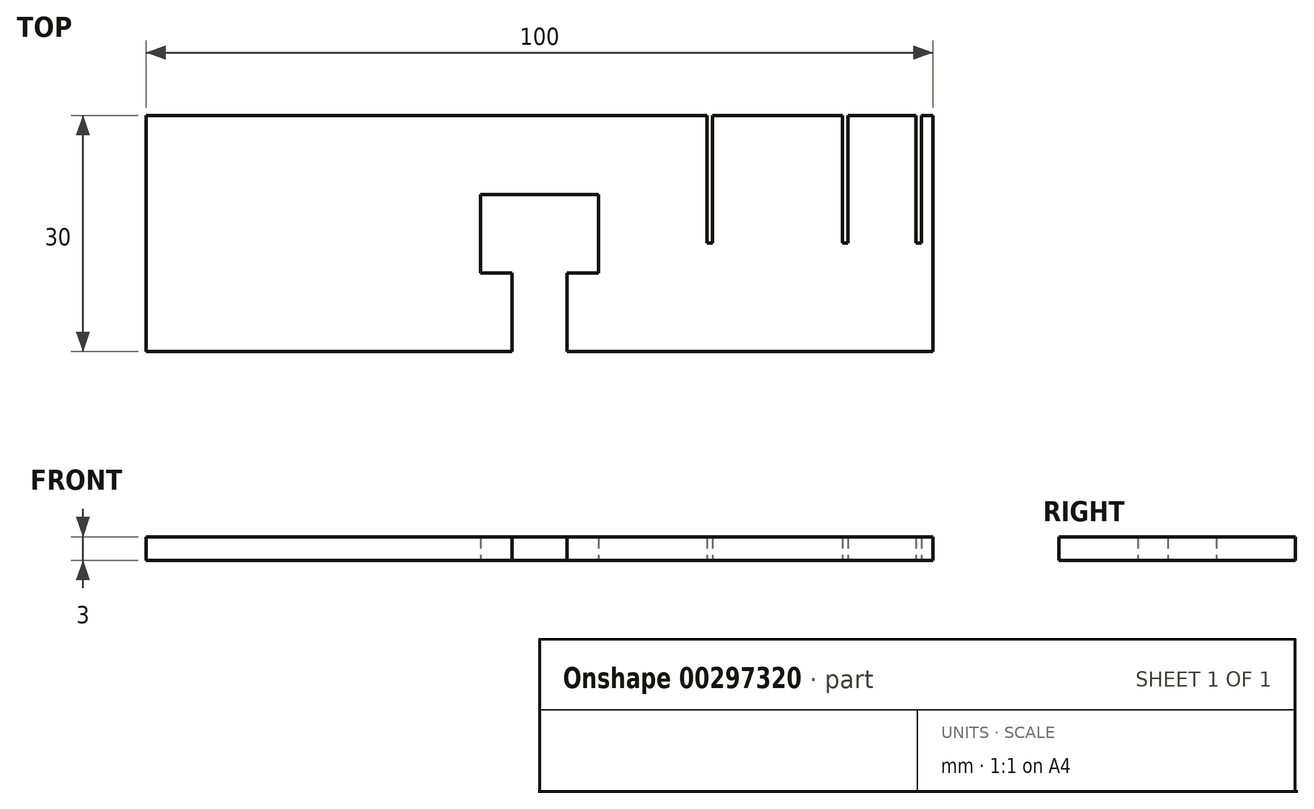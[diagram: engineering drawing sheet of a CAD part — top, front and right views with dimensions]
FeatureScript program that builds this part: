
annotation { "Feature Type Name" : "Feature", "Feature Type Description" : "" }
export const myFeature = defineFeature(function(context is Context, id is Id, definition is map)
    precondition{}
    {
        {
            var Q0;
            Q0=qCreatedBy(makeId("Top.planeOp"),FACE);
            var sketch = newSketch(context, id + "F0", { "sketchPlane" : qUnion([Q0])});
            skLineSegment(sketch, "E0.bottom", {"start": v(50, -15) * mm, "end": v(-50, -15) * mm});
            skLineSegment(sketch, "E0.top", {"start": v(50, 15) * mm, "end": v(-50, 15) * mm});
            skLineSegment(sketch, "E0.left", {"start": v(50, -15) * mm, "end": v(50, 15) * mm});
            skLineSegment(sketch, "E0.right", {"start": v(-50, -15) * mm, "end": v(-50, 15) * mm});
            skPoint(sketch, "E0.middle", {"position": v(0, 0) * mm});
            skSolve(sketch);
        }
        {
            var Q0;
            Q0=qCreatedBy(makeId("Top.planeOp"),FACE);
            var sketch = newSketch(context, id + "F1", { "sketchPlane" : qUnion([Q0])});
            skPoint(sketch, "E1.middle", {"position": v(0, 0) * mm});
            skLineSegment(sketch, "E2.bottom", {"start": v(7.5, -5) * mm, "end": v(-7.5, -5) * mm});
            skLineSegment(sketch, "E2.top", {"start": v(7.5, 5) * mm, "end": v(-7.5, 5) * mm});
            skLineSegment(sketch, "E2.left", {"start": v(7.5, -5) * mm, "end": v(7.5, 5) * mm});
            skLineSegment(sketch, "E2.right", {"start": v(-7.5, -5) * mm, "end": v(-7.5, 5) * mm});
            skLineSegment(sketch, "E3.bottom", {"start": v(-3.5, -5) * mm, "end": v(3.5, -5) * mm});
            skLineSegment(sketch, "E3.top", {"start": v(-3.5, -20) * mm, "end": v(3.5, -20) * mm});
            skLineSegment(sketch, "E3.left", {"start": v(-3.5, -5) * mm, "end": v(-3.5, -20) * mm});
            skLineSegment(sketch, "E3.right", {"start": v(3.5, -5) * mm, "end": v(3.5, -20) * mm});
            skLineSegment(sketch, "E4.bottom", {"start": v(21.3, -1.2) * mm, "end": v(22, -1.2) * mm});
            skLineSegment(sketch, "E4.top", {"start": v(21.3, 27.79) * mm, "end": v(22, 27.79) * mm});
            skLineSegment(sketch, "E4.left", {"start": v(21.3, -1.2) * mm, "end": v(21.3, 27.79) * mm});
            skLineSegment(sketch, "E4.right", {"start": v(22, -1.2) * mm, "end": v(22, 27.79) * mm});
            skLineSegment(sketch, "E5.bottom", {"start": v(47.8, -1.2) * mm, "end": v(48.5, -1.2) * mm});
            skLineSegment(sketch, "E5.top", {"start": v(47.8, 38.42) * mm, "end": v(48.5, 38.42) * mm});
            skLineSegment(sketch, "E5.left", {"start": v(47.8, -1.2) * mm, "end": v(47.8, 38.42) * mm});
            skLineSegment(sketch, "E5.right", {"start": v(48.5, -1.2) * mm, "end": v(48.5, 38.42) * mm});
            skLineSegment(sketch, "E6.bottom", {"start": v(38.47, -1.2) * mm, "end": v(39.17, -1.2) * mm});
            skLineSegment(sketch, "E6.top", {"start": v(38.47, 25.3) * mm, "end": v(39.17, 25.3) * mm});
            skLineSegment(sketch, "E6.left", {"start": v(38.47, -1.2) * mm, "end": v(38.47, 25.3) * mm});
            skLineSegment(sketch, "E6.right", {"start": v(39.17, -1.2) * mm, "end": v(39.17, 25.3) * mm});
            skSolve(sketch);
        }
        {
            var Q0;
            Q0=qSketchRegion(id+"F0",true);
            extrude(context, id + "F2", {"entities" : qUnion([Q0]), "depth" : 3 * mm});
        }
        {
            var Q0;
            Q0=qSketchRegion(id+"F1",true);
            extrude(context, id + "F3", {"entities" : qUnion([Q0]), "operationType" : NewBodyOperationType.REMOVE, "depth" : 4 * mm});
        }
    });
